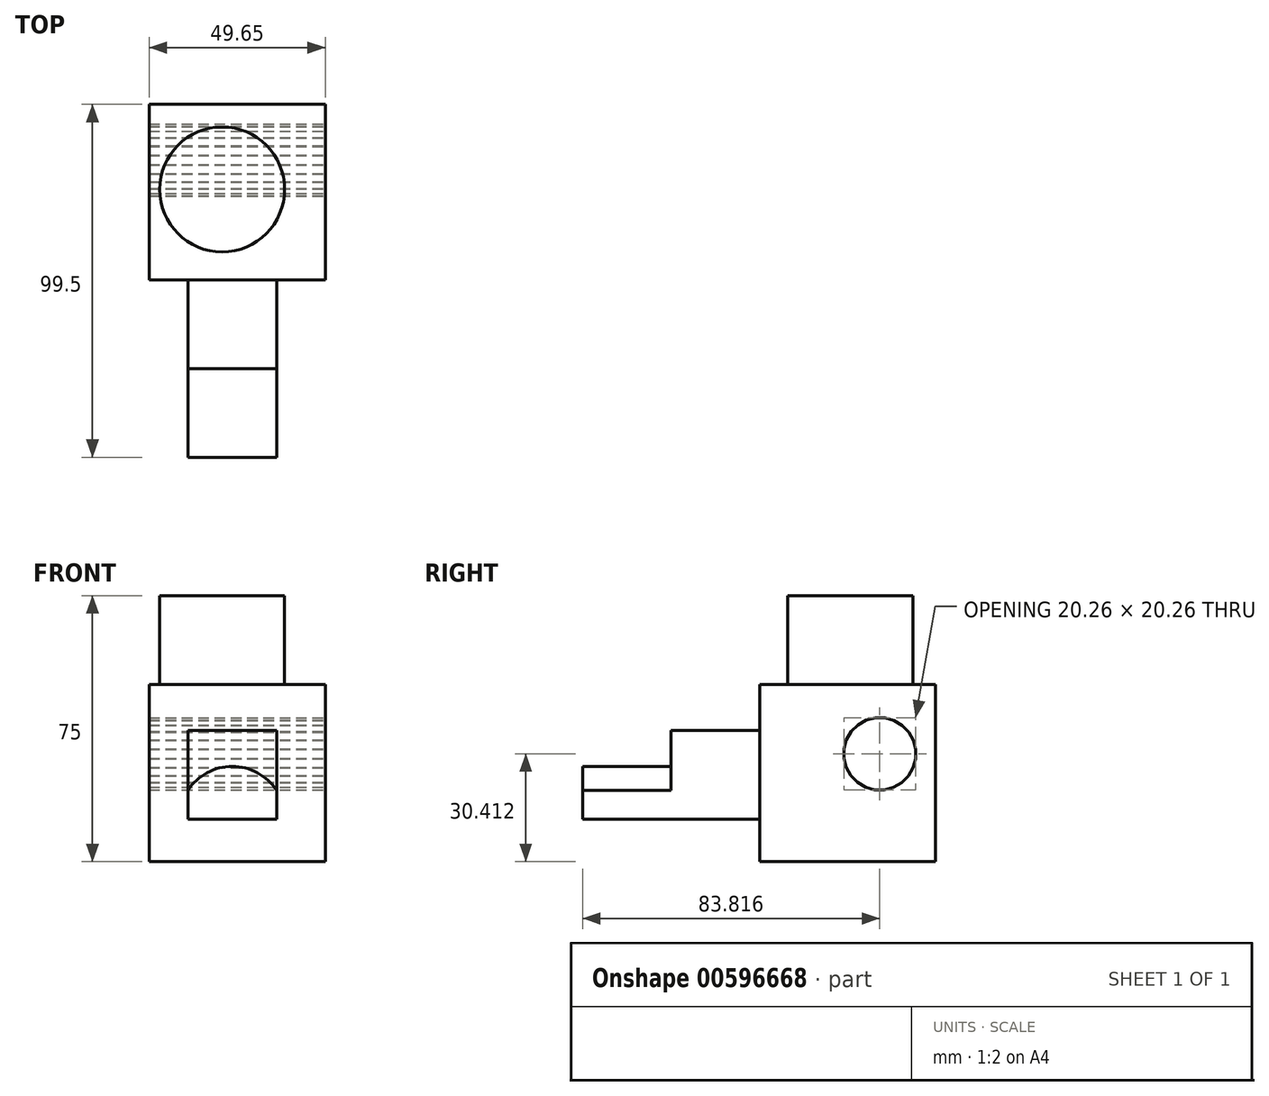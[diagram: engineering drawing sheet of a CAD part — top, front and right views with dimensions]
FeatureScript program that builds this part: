
annotation { "Feature Type Name" : "Feature", "Feature Type Description" : "" }
export const myFeature = defineFeature(function(context is Context, id is Id, definition is map)
    precondition{}
    {
        {
            var Q0;
            Q0=qCreatedBy(makeId("Top.planeOp"),FACE);
            var sketch = newSketch(context, id + "F0", { "sketchPlane" : qUnion([Q0])});
            skLineSegment(sketch, "E0.bottom", {"start": v(0, 0) * mm, "end": v(49.65, 0) * mm});
            skLineSegment(sketch, "E0.top", {"start": v(0, 49.5) * mm, "end": v(49.65, 49.5) * mm});
            skLineSegment(sketch, "E0.left", {"start": v(0, 0) * mm, "end": v(0, 49.5) * mm});
            skLineSegment(sketch, "E0.right", {"start": v(49.65, 0) * mm, "end": v(49.65, 49.5) * mm});
            skSolve(sketch);
        }
        {
            var Q0;
            Q0 = qSketchRegion(id + "F0", true);
            extrude(context, id + "F1", {"entities" : qUnion([Q0]), "depth" : 50 * mm, "offsetDistance" : 25 * mm});
        }
        {
            var Q0;
            Q0=makeQuery(id+"F1.opExtrude","SWEPT_FACE",FACE,{"disambiguationData":[OSD([sQuery(id+"F0.wireOp",EDGE,"E0.bottom")])]});
            var sketch = newSketch(context, id + "F2", { "sketchPlane" : qUnion([Q0])});
            skLineSegment(sketch, "E1.bottom", {"start": v(10.9, 36.96) * mm, "end": v(35.9, 36.96) * mm});
            skLineSegment(sketch, "E1.top", {"start": v(10.9, 11.96) * mm, "end": v(35.9, 11.96) * mm});
            skLineSegment(sketch, "E1.left", {"start": v(10.9, 36.96) * mm, "end": v(10.9, 11.96) * mm});
            skLineSegment(sketch, "E1.right", {"start": v(35.9, 36.96) * mm, "end": v(35.9, 11.96) * mm});
            skSolve(sketch);
        }
        {
            var Q0;
            Q0=makeQuery(id+"F2.imprint","IMPRINT",FACE,{"disambiguationData":[TD([[makeQuery(id+"F2.imprint","IMPRINT",EDGE,{"derivedFrom":sQuery(id+"F2.wireOp",EDGE,"E1.bottom")}),-1.0]])]});
            extrude(context, id + "F3", {"entities" : qUnion([Q0]), "operationType" : NewBodyOperationType.ADD, "depth" : 25 * mm, "offsetDistance" : 25 * mm});
        }
        {
            var Q0;
            Q0=makeQuery(id+"F1.opExtrude","CAP_FACE",FACE,{"disambiguationData":[OSD([sQuery(id+"F0.wireOp",EDGE,"E0.bottom"),sQuery(id+"F0.wireOp",EDGE,"E0.top"),sQuery(id+"F0.wireOp",EDGE,"E0.left"),sQuery(id+"F0.wireOp",EDGE,"E0.right")])],"isStart":false});
            var sketch = newSketch(context, id + "F4", { "sketchPlane" : qUnion([Q0])});
            skCircle(sketch, "E2", {"center": v(20.55, 25.5) * mm, "radius": 17.62 * mm});
            skSolve(sketch);
        }
        {
            var Q0;
            Q0=makeQuery(id+"F4.imprint","IMPRINT",FACE,{"disambiguationData":[TD([[makeQuery(id+"F4.imprint","IMPRINT",EDGE,{"derivedFrom":sQuery(id+"F4.wireOp",EDGE,"E2")}),1.0]])]});
            extrude(context, id + "F5", {"entities" : qUnion([Q0]), "operationType" : NewBodyOperationType.ADD, "depth" : 25 * mm, "offsetDistance" : 25 * mm});
        }
        {
            var Q0;
            Q0=makeQuery(id+"F1.opExtrude","SWEPT_FACE",FACE,{"disambiguationData":[OSD([sQuery(id+"F0.wireOp",EDGE,"E0.right")])]});
            var sketch = newSketch(context, id + "F6", { "sketchPlane" : qUnion([Q0])});
            skCircle(sketch, "E3.cCircle", {"center": v(33.82, 30.41) * mm, "radius": 10.12 * mm, "construction": true});
            skLineSegment(sketch, "E3.0", {"start": v(24.35, 26.58) * mm, "end": v(23.68, 29.16) * mm});
            skLineSegment(sketch, "E3.1", {"start": v(23.68, 29.16) * mm, "end": v(23.7, 31.83) * mm});
            skLineSegment(sketch, "E3.2", {"start": v(23.7, 31.83) * mm, "end": v(24.42, 34.4) * mm});
            skLineSegment(sketch, "E3.3", {"start": v(24.42, 34.4) * mm, "end": v(25.77, 36.7) * mm});
            skLineSegment(sketch, "E3.4", {"start": v(25.77, 36.7) * mm, "end": v(27.67, 38.56) * mm});
            skLineSegment(sketch, "E3.5", {"start": v(27.67, 38.56) * mm, "end": v(29.99, 39.87) * mm});
            skLineSegment(sketch, "E3.6", {"start": v(29.99, 39.87) * mm, "end": v(32.56, 40.54) * mm});
            skLineSegment(sketch, "E3.7", {"start": v(32.56, 40.54) * mm, "end": v(35.23, 40.52) * mm});
            skLineSegment(sketch, "E3.8", {"start": v(35.23, 40.52) * mm, "end": v(37.8, 39.81) * mm});
            skLineSegment(sketch, "E3.9", {"start": v(37.8, 39.81) * mm, "end": v(40.1, 38.46) * mm});
            skLineSegment(sketch, "E3.10", {"start": v(40.1, 38.46) * mm, "end": v(41.96, 36.56) * mm});
            skLineSegment(sketch, "E3.11", {"start": v(41.96, 36.56) * mm, "end": v(43.28, 34.24) * mm});
            skLineSegment(sketch, "E3.12", {"start": v(43.28, 34.24) * mm, "end": v(43.95, 31.66) * mm});
            skLineSegment(sketch, "E3.13", {"start": v(43.95, 31.66) * mm, "end": v(43.92, 29) * mm});
            skLineSegment(sketch, "E3.14", {"start": v(43.92, 29) * mm, "end": v(43.21, 26.43) * mm});
            skLineSegment(sketch, "E3.15", {"start": v(43.21, 26.43) * mm, "end": v(41.86, 24.13) * mm});
            skLineSegment(sketch, "E3.16", {"start": v(41.86, 24.13) * mm, "end": v(39.96, 22.26) * mm});
            skLineSegment(sketch, "E3.17", {"start": v(39.96, 22.26) * mm, "end": v(37.65, 20.95) * mm});
            skLineSegment(sketch, "E3.18", {"start": v(37.65, 20.95) * mm, "end": v(35.07, 20.28) * mm});
            skLineSegment(sketch, "E3.19", {"start": v(35.07, 20.28) * mm, "end": v(32.4, 20.3) * mm});
            skLineSegment(sketch, "E3.20", {"start": v(32.4, 20.3) * mm, "end": v(29.83, 21.01) * mm});
            skLineSegment(sketch, "E3.21", {"start": v(29.83, 21.01) * mm, "end": v(27.54, 22.36) * mm});
            skLineSegment(sketch, "E3.22", {"start": v(27.54, 22.36) * mm, "end": v(25.67, 24.26) * mm});
            skLineSegment(sketch, "E3.23", {"start": v(25.67, 24.26) * mm, "end": v(24.35, 26.58) * mm});
            skPoint(sketch, "E3.0.midPoint", {"position": v(24.02, 27.87) * mm});
            skCircle(sketch, "E4.cCircle", {"center": v(33.82, 30.41) * mm, "radius": 19.77 * mm, "construction": true});
            skLineSegment(sketch, "E4.0", {"start": v(14.4, 26.37) * mm, "end": v(14.01, 29.38) * mm});
            skLineSegment(sketch, "E4.1", {"start": v(14.01, 29.38) * mm, "end": v(14.09, 32.41) * mm});
            skLineSegment(sketch, "E4.2", {"start": v(14.09, 32.41) * mm, "end": v(14.62, 35.4) * mm});
            skLineSegment(sketch, "E4.3", {"start": v(14.62, 35.4) * mm, "end": v(15.6, 38.27) * mm});
            skLineSegment(sketch, "E4.4", {"start": v(15.6, 38.27) * mm, "end": v(17.02, 40.96) * mm});
            skLineSegment(sketch, "E4.5", {"start": v(17.02, 40.96) * mm, "end": v(18.83, 43.4) * mm});
            skLineSegment(sketch, "E4.6", {"start": v(18.83, 43.4) * mm, "end": v(20.99, 45.53) * mm});
            skLineSegment(sketch, "E4.7", {"start": v(20.99, 45.53) * mm, "end": v(23.45, 47.31) * mm});
            skLineSegment(sketch, "E4.8", {"start": v(23.45, 47.31) * mm, "end": v(26.15, 48.7) * mm});
            skLineSegment(sketch, "E4.9", {"start": v(26.15, 48.7) * mm, "end": v(29.03, 49.66) * mm});
            skLineSegment(sketch, "E4.10", {"start": v(29.03, 49.66) * mm, "end": v(32.02, 50.16) * mm});
            skLineSegment(sketch, "E4.11", {"start": v(32.02, 50.16) * mm, "end": v(35.06, 50.2) * mm});
            skLineSegment(sketch, "E4.12", {"start": v(35.06, 50.2) * mm, "end": v(38.06, 49.78) * mm});
            skLineSegment(sketch, "E4.13", {"start": v(38.06, 49.78) * mm, "end": v(40.97, 48.9) * mm});
            skLineSegment(sketch, "E4.14", {"start": v(40.97, 48.9) * mm, "end": v(43.71, 47.6) * mm});
            skLineSegment(sketch, "E4.15", {"start": v(43.71, 47.6) * mm, "end": v(46.22, 45.88) * mm});
            skLineSegment(sketch, "E4.16", {"start": v(46.22, 45.88) * mm, "end": v(48.43, 43.81) * mm});
            skLineSegment(sketch, "E4.17", {"start": v(48.43, 43.81) * mm, "end": v(50.3, 41.42) * mm});
            skLineSegment(sketch, "E4.18", {"start": v(50.3, 41.42) * mm, "end": v(51.8, 38.77) * mm});
            skLineSegment(sketch, "E4.19", {"start": v(51.8, 38.77) * mm, "end": v(52.86, 35.93) * mm});
            skLineSegment(sketch, "E4.20", {"start": v(52.86, 35.93) * mm, "end": v(53.48, 32.96) * mm});
            skLineSegment(sketch, "E4.21", {"start": v(53.48, 32.96) * mm, "end": v(53.64, 29.93) * mm});
            skLineSegment(sketch, "E4.22", {"start": v(53.64, 29.93) * mm, "end": v(53.33, 26.9) * mm});
            skLineSegment(sketch, "E4.23", {"start": v(53.33, 26.9) * mm, "end": v(52.57, 23.97) * mm});
            skLineSegment(sketch, "E4.24", {"start": v(52.57, 23.97) * mm, "end": v(51.37, 21.18) * mm});
            skLineSegment(sketch, "E4.25", {"start": v(51.37, 21.18) * mm, "end": v(49.75, 18.61) * mm});
            skLineSegment(sketch, "E4.26", {"start": v(49.75, 18.61) * mm, "end": v(47.76, 16.32) * mm});
            skLineSegment(sketch, "E4.27", {"start": v(47.76, 16.32) * mm, "end": v(45.45, 14.35) * mm});
            skLineSegment(sketch, "E4.28", {"start": v(45.45, 14.35) * mm, "end": v(42.86, 12.77) * mm});
            skLineSegment(sketch, "E4.29", {"start": v(42.86, 12.77) * mm, "end": v(40.06, 11.6) * mm});
            skLineSegment(sketch, "E4.30", {"start": v(40.06, 11.6) * mm, "end": v(37.11, 10.86) * mm});
            skLineSegment(sketch, "E4.31", {"start": v(37.11, 10.86) * mm, "end": v(34.1, 10.58) * mm});
            skLineSegment(sketch, "E4.32", {"start": v(34.1, 10.58) * mm, "end": v(31.06, 10.77) * mm});
            skLineSegment(sketch, "E4.33", {"start": v(31.06, 10.77) * mm, "end": v(28.1, 11.43) * mm});
            skLineSegment(sketch, "E4.34", {"start": v(28.1, 11.43) * mm, "end": v(25.26, 12.52) * mm});
            skLineSegment(sketch, "E4.35", {"start": v(25.26, 12.52) * mm, "end": v(22.63, 14.04) * mm});
            skLineSegment(sketch, "E4.36", {"start": v(22.63, 14.04) * mm, "end": v(20.27, 15.93) * mm});
            skLineSegment(sketch, "E4.37", {"start": v(20.27, 15.93) * mm, "end": v(18.21, 18.17) * mm});
            skLineSegment(sketch, "E4.38", {"start": v(18.21, 18.17) * mm, "end": v(16.53, 20.7) * mm});
            skLineSegment(sketch, "E4.39", {"start": v(16.53, 20.7) * mm, "end": v(15.25, 23.45) * mm});
            skLineSegment(sketch, "E4.40", {"start": v(15.25, 23.45) * mm, "end": v(14.4, 26.37) * mm});
            skPoint(sketch, "E4.0.midPoint", {"position": v(14.2, 27.87) * mm});
            skSolve(sketch);
        }
        {
            var Q0;
            Q0=makeQuery(id+"F6.imprint","IMPRINT",FACE,{"disambiguationData":[TD([[makeQuery(id+"F6.imprint","IMPRINT",EDGE,{"derivedFrom":sQuery(id+"F6.wireOp",EDGE,"E3.0")}),-1.0]])]});
            extrude(context, id + "F7", {"entities" : qUnion([Q0]), "operationType" : NewBodyOperationType.ADD, "depth" : 25 * mm, "offsetDistance" : 25 * mm});
        }
        {
            var Q0;
            Q0=makeQuery(id+"F7.opExtrude","CAP_FACE",FACE,{"disambiguationData":[OSD([sQuery(id+"F6.wireOp",EDGE,"E3.0"),sQuery(id+"F6.wireOp",EDGE,"E3.1"),sQuery(id+"F6.wireOp",EDGE,"E3.2"),sQuery(id+"F6.wireOp",EDGE,"E3.3"),sQuery(id+"F6.wireOp",EDGE,"E3.4"),sQuery(id+"F6.wireOp",EDGE,"E3.5"),sQuery(id+"F6.wireOp",EDGE,"E3.6"),sQuery(id+"F6.wireOp",EDGE,"E3.7"),sQuery(id+"F6.wireOp",EDGE,"E3.8"),sQuery(id+"F6.wireOp",EDGE,"E3.9"),sQuery(id+"F6.wireOp",EDGE,"E3.10"),sQuery(id+"F6.wireOp",EDGE,"E3.11"),sQuery(id+"F6.wireOp",EDGE,"E3.12"),sQuery(id+"F6.wireOp",EDGE,"E3.13"),sQuery(id+"F6.wireOp",EDGE,"E3.14"),sQuery(id+"F6.wireOp",EDGE,"E3.15"),sQuery(id+"F6.wireOp",EDGE,"E3.16"),sQuery(id+"F6.wireOp",EDGE,"E3.17"),sQuery(id+"F6.wireOp",EDGE,"E3.18"),sQuery(id+"F6.wireOp",EDGE,"E3.19"),sQuery(id+"F6.wireOp",EDGE,"E3.20"),sQuery(id+"F6.wireOp",EDGE,"E3.21"),sQuery(id+"F6.wireOp",EDGE,"E3.22"),sQuery(id+"F6.wireOp",EDGE,"E3.23")])],"isStart":false});
            extrude(context, id + "F8", {"entities" : qUnion([Q0]), "operationType" : NewBodyOperationType.ADD, "depth" : 25 * mm, "offsetDistance" : 25 * mm});
        }
        {
            var Q0;
            Q0=makeQuery(id+"F8.opExtrude","CAP_FACE",FACE,{"disambiguationData":[OSD([sQuery(id+"F6.wireOp",EDGE,"E3.0"),sQuery(id+"F6.wireOp",EDGE,"E3.1"),sQuery(id+"F6.wireOp",EDGE,"E3.2"),sQuery(id+"F6.wireOp",EDGE,"E3.3"),sQuery(id+"F6.wireOp",EDGE,"E3.4"),sQuery(id+"F6.wireOp",EDGE,"E3.5"),sQuery(id+"F6.wireOp",EDGE,"E3.6"),sQuery(id+"F6.wireOp",EDGE,"E3.7"),sQuery(id+"F6.wireOp",EDGE,"E3.8"),sQuery(id+"F6.wireOp",EDGE,"E3.9"),sQuery(id+"F6.wireOp",EDGE,"E3.10"),sQuery(id+"F6.wireOp",EDGE,"E3.11"),sQuery(id+"F6.wireOp",EDGE,"E3.12"),sQuery(id+"F6.wireOp",EDGE,"E3.13"),sQuery(id+"F6.wireOp",EDGE,"E3.14"),sQuery(id+"F6.wireOp",EDGE,"E3.15"),sQuery(id+"F6.wireOp",EDGE,"E3.16"),sQuery(id+"F6.wireOp",EDGE,"E3.17"),sQuery(id+"F6.wireOp",EDGE,"E3.18"),sQuery(id+"F6.wireOp",EDGE,"E3.19"),sQuery(id+"F6.wireOp",EDGE,"E3.20"),sQuery(id+"F6.wireOp",EDGE,"E3.21"),sQuery(id+"F6.wireOp",EDGE,"E3.22"),sQuery(id+"F6.wireOp",EDGE,"E3.23")])],"isStart":false});
            extrude(context, id + "F9", {"entities" : qUnion([Q0]), "operationType" : NewBodyOperationType.REMOVE, "oppositeDirection" : true, "depth" : 55 * mm, "offsetDistance" : 25 * mm});
        }
        {
            var Q0;
            Q0=makeQuery(id+"F9.boolean.opBoolean","COPY",FACE,{"derivedFrom":makeQuery(id+"F9.opExtrude","CAP_FACE",FACE,{"disambiguationData":[OSD([sQuery(id+"F6.wireOp",EDGE,"E3.0"),sQuery(id+"F6.wireOp",EDGE,"E3.1"),sQuery(id+"F6.wireOp",EDGE,"E3.2"),sQuery(id+"F6.wireOp",EDGE,"E3.3"),sQuery(id+"F6.wireOp",EDGE,"E3.4"),sQuery(id+"F6.wireOp",EDGE,"E3.5"),sQuery(id+"F6.wireOp",EDGE,"E3.6"),sQuery(id+"F6.wireOp",EDGE,"E3.7"),sQuery(id+"F6.wireOp",EDGE,"E3.8"),sQuery(id+"F6.wireOp",EDGE,"E3.9"),sQuery(id+"F6.wireOp",EDGE,"E3.10"),sQuery(id+"F6.wireOp",EDGE,"E3.11"),sQuery(id+"F6.wireOp",EDGE,"E3.12"),sQuery(id+"F6.wireOp",EDGE,"E3.13"),sQuery(id+"F6.wireOp",EDGE,"E3.14"),sQuery(id+"F6.wireOp",EDGE,"E3.15"),sQuery(id+"F6.wireOp",EDGE,"E3.16"),sQuery(id+"F6.wireOp",EDGE,"E3.17"),sQuery(id+"F6.wireOp",EDGE,"E3.18"),sQuery(id+"F6.wireOp",EDGE,"E3.19"),sQuery(id+"F6.wireOp",EDGE,"E3.20"),sQuery(id+"F6.wireOp",EDGE,"E3.21"),sQuery(id+"F6.wireOp",EDGE,"E3.22"),sQuery(id+"F6.wireOp",EDGE,"E3.23")])],"isStart":false})});
            extrude(context, id + "F10", {"entities" : qUnion([Q0]), "operationType" : NewBodyOperationType.ADD, "depth" : 55 * mm, "offsetDistance" : 25 * mm});
        }
        {
            var Q0;
            Q0=makeQuery(id+"F10.opExtrude","CAP_FACE",FACE,{"disambiguationData":[OSD([sQuery(id+"F6.wireOp",EDGE,"E3.0"),sQuery(id+"F6.wireOp",EDGE,"E3.1"),sQuery(id+"F6.wireOp",EDGE,"E3.2"),sQuery(id+"F6.wireOp",EDGE,"E3.3"),sQuery(id+"F6.wireOp",EDGE,"E3.4"),sQuery(id+"F6.wireOp",EDGE,"E3.5"),sQuery(id+"F6.wireOp",EDGE,"E3.6"),sQuery(id+"F6.wireOp",EDGE,"E3.7"),sQuery(id+"F6.wireOp",EDGE,"E3.8"),sQuery(id+"F6.wireOp",EDGE,"E3.9"),sQuery(id+"F6.wireOp",EDGE,"E3.10"),sQuery(id+"F6.wireOp",EDGE,"E3.11"),sQuery(id+"F6.wireOp",EDGE,"E3.12"),sQuery(id+"F6.wireOp",EDGE,"E3.13"),sQuery(id+"F6.wireOp",EDGE,"E3.14"),sQuery(id+"F6.wireOp",EDGE,"E3.15"),sQuery(id+"F6.wireOp",EDGE,"E3.16"),sQuery(id+"F6.wireOp",EDGE,"E3.17"),sQuery(id+"F6.wireOp",EDGE,"E3.18"),sQuery(id+"F6.wireOp",EDGE,"E3.19"),sQuery(id+"F6.wireOp",EDGE,"E3.20"),sQuery(id+"F6.wireOp",EDGE,"E3.21"),sQuery(id+"F6.wireOp",EDGE,"E3.22"),sQuery(id+"F6.wireOp",EDGE,"E3.23")])],"isStart":false});
            extrude(context, id + "F11", {"entities" : qUnion([Q0]), "operationType" : NewBodyOperationType.REMOVE, "oppositeDirection" : true, "depth" : 100 * mm, "offsetDistance" : 25 * mm});
        }
        {
            var Q0;
            Q0=makeQuery(id+"F3.opExtrude","CAP_FACE",FACE,{"disambiguationData":[OSD([sQuery(id+"F2.wireOp",EDGE,"E1.bottom"),sQuery(id+"F2.wireOp",EDGE,"E1.top"),sQuery(id+"F2.wireOp",EDGE,"E1.left"),sQuery(id+"F2.wireOp",EDGE,"E1.right")])],"isStart":false});
            var sketch = newSketch(context, id + "F12", { "sketchPlane" : qUnion([Q0])});
            skCircle(sketch, "E5", {"center": v(23.4, 11.96) * mm, "radius": 14.91 * mm});
            skSolve(sketch);
        }
        {
            var Q0;
            {var subQ5=makeQuery(id+"F3.opExtrude","CAP_EDGE",EDGE,{"disambiguationData":[OSD([sQuery(id+"F2.wireOp",EDGE,"E1.top")])],"isStart":false});Q0=makeQuery(id+"F12.imprint","IMPRINT",FACE,{"disambiguationData":[TD([[makeQuery(id+"F12.imprint","IMPRINT",EDGE,{"derivedFrom":subQ5}),1.0]])]});}
            extrude(context, id + "F13", {"entities" : qUnion([Q0]), "operationType" : NewBodyOperationType.ADD, "depth" : 25 * mm, "offsetDistance" : 25 * mm});
        }
    });
